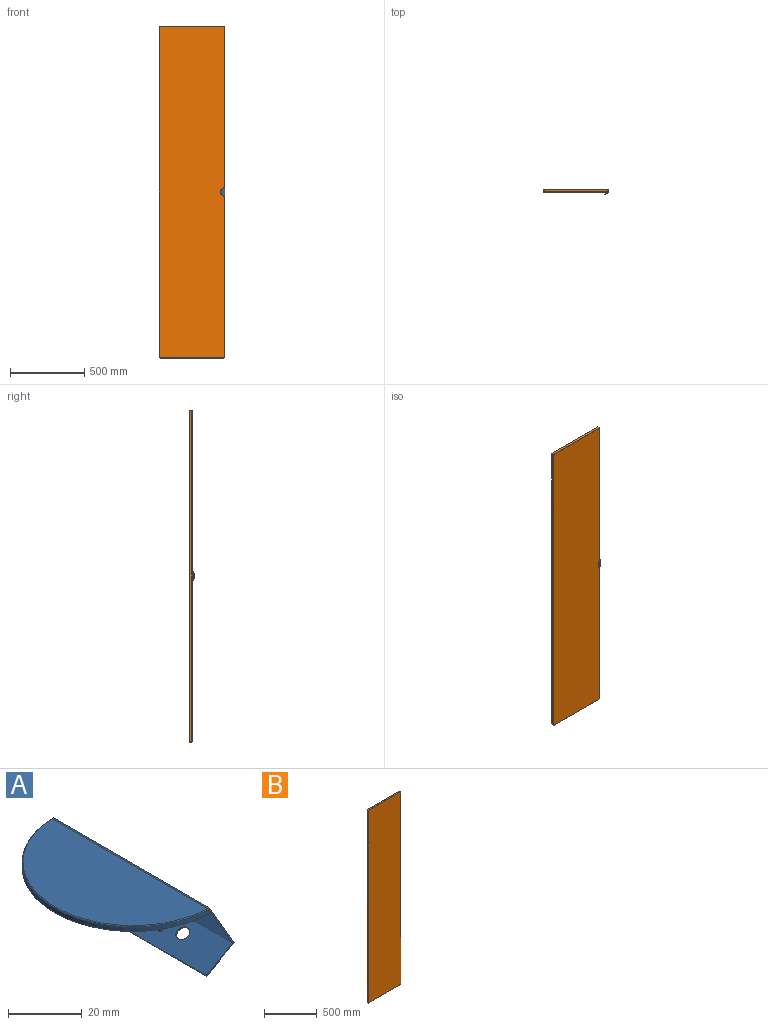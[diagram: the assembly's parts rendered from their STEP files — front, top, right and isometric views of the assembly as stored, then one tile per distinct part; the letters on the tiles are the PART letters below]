
ASSEMBLY  parts=2 mates=1
PART A: 26 faces, bbox 38.7x60x22 mm
  f0: plane 1.52x0.88mm, normal (0.87,0,0.5), area 0mm2, adj f2,f4,f17
  f1: plane 1.52x0.88mm, normal (0.87,0,0.5), area 0mm2, adj f2,f4,f19
  f2: cylinder r=30mm len=60mm, axis (0,0,-1), area 139.6mm2, adj f0,f1,f4,f5
  f3: plane 59.46x28.6mm, normal (0,0,1), area 1321.6mm2, adj f5,f15
  f4: cone r=30mm half-angle=45deg, axis (0,0,1), area 33.1mm2, adj f0,f1,f2,f6,f16
  f5: cone r=29.75mm half-angle=45deg, axis (0,0,-1), area 32.4mm2, adj f2,f3,f15
  f6: plane 59.5x29.75mm, normal (0,0,-1), area 945.2mm2, adj f4,f8,f9,f10,f16
  f7: plane 46x10mm, normal (0.5,0,-0.87), area 496.8mm2, adj f8,f9,f10,f12,f14,f16
  f8: plane 41.42x5.77mm, normal (-1,0,0), area 239.2mm2, adj f6,f7,f9,f10
  f9: cylinder r=23mm len=10mm, axis (0,0,1), area 30.4mm2, adj f6,f7,f8
  f10: cylinder r=23mm len=10mm, axis (0,0,1), area 30.4mm2, adj f6,f7,f8
  f11: cone r=0mm half-angle=59deg, axis (0.5,0,-0.87), area 10mm2, adj f12
  f12: cylinder r=1.65mm len=4.85mm, axis (0.5,0,-0.87), area 38.4mm2, adj f7,f11
  f13: cone r=0mm half-angle=59deg, axis (0.5,0,-0.87), area 10mm2, adj f14
  f14: cylinder r=1.65mm len=4.85mm, axis (0.5,0,-0.87), area 38.4mm2, adj f7,f13
  f15: plane 59.97x0.25mm, normal (0.87,0,0.5), area 17.2mm2, adj f3,f5,f18
  f16: plane 59.97x14.09mm, normal (-0.87,0,-0.5), area 959.5mm2, adj f4,f6,f7,f17,f19,f23
  f17: plane 22.04x10.64mm, normal (0,1,0), area 15mm2, adj f0,f16,f18,f20,f21,f22,f23
  f18: plane 59.97x0.43mm, normal (-0.5,0,0.87), area 30mm2, adj f15,f17,f19,f20
  f19: plane 22.04x10.64mm, normal (0,-1,0), area 15mm2, adj f1,f16,f18,f20,f21,f22,f23
  f20: plane 59.97x16.04mm, normal (0.87,0,0.5), area 1110.6mm2, adj f17,f18,f19,f22
  f21: plane 59.97x0.43mm, normal (-0.87,0,-0.5), area 30mm2, adj f17,f19,f22,f23
  f22: plane 59.97x10.39mm, normal (0.5,0,-0.87), area 694.5mm2, adj f17,f19,f20,f21,f24,f25
  f23: plane 59.97x9.96mm, normal (-0.5,0,0.87), area 664.5mm2, adj f16,f17,f19,f21,f24,f25
  f24: cylinder r=2mm len=4mm, axis (0.5,0,-0.87), area 6.3mm2, adj f22,f23
  f25: cylinder r=2mm len=4mm, axis (0.5,0,-0.87), area 6.3mm2, adj f22,f23
PART B: 18 faces, bbox 440.8x16x2240.8 mm
  f0: plane 430x15mm, normal (0,0,1), area 6450mm2, adj f5,f6,f9,f10
  f1: plane 2230x15mm, normal (-1,0,0), area 33450mm2, adj f5,f6,f7,f13
  f2: plane 430x15mm, normal (0,0,-1), area 6450mm2, adj f5,f7,f8,f17
  f3: plane 2230x15mm, normal (1,0,0), area 33450mm2, adj f5,f8,f9,f14
  f4: plane 2238x438mm, normal (0,-1,0), area 980230.3mm2, adj f10,f11,f12,f13,f14,f15,f16,f17
  f5: plane 2240x440mm, normal (0,1,0), area 985578.5mm2, adj f0,f1,f2,f3,f6,f7,f8,f9
  f6: cylinder r=5mm len=15mm, axis (0,-1,0), area 117.8mm2, adj f0,f1,f5,f11
  f7: cylinder r=5mm len=15mm, axis (0,1,0), area 117.8mm2, adj f1,f2,f5,f15
  f8: cylinder r=5mm len=15mm, axis (0,-1,0), area 117.8mm2, adj f2,f3,f5,f16
  f9: cylinder r=5mm len=15mm, axis (0,1,0), area 117.8mm2, adj f0,f3,f5,f12
  f10: cylinder r=1mm len=430mm, axis (1,0,0), area 675.4mm2, adj f0,f4,f11,f12
  f11: torus R=4mm, axis (0,-1,0), area 11.4mm2, adj f4,f6,f10,f13
  f12: torus R=4mm, axis (0,-1,0), area 11.4mm2, adj f4,f9,f10,f14
  f13: cylinder r=1mm len=2230mm, axis (0,0,1), area 3502.9mm2, adj f1,f4,f11,f15
  f14: cylinder r=1mm len=2230mm, axis (0,0,-1), area 3502.9mm2, adj f3,f4,f12,f16
  f15: torus R=4mm, axis (0,-1,0), area 11.4mm2, adj f4,f7,f13,f17
  f16: torus R=4mm, axis (0,-1,0), area 11.4mm2, adj f4,f8,f14,f17
  f17: cylinder r=1mm len=430mm, axis (-1,0,0), area 675.4mm2, adj f2,f4,f15,f16
PLACE A rot(axis=(0.94,0.25,0.25),93.8deg) t=(-475.34,39.61,672.85)mm
PLACE B t=(-693.85,55.11,-132.41)mm
MATE fastened A.f16 <-> B.f3  axis (-1,0,0) through (-475.34,47.61,672.85)mm
